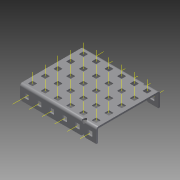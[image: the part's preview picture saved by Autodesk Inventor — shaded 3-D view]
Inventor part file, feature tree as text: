
AUTODESK INVENTOR PART (.ipt)
format: ipt  version: 2015 (Build 190159000, 159)  size: 2,469,376 bytes
history: native  units: in
note: dims shown in document units (in); Inventor stores cm internally (conversion verified against a paired STEP export)
features: other x48, pattern_linear x2, sheet_metal_op x1, extrude x1, imported_body x1, sketch x1
ambient origin geometry x8: Origin, YZ Plane, XZ Plane, XY Plane, X Axis, Y Axis, Z Axis, Center Point
bodies: Body1 (feature_tree)
feature tree (54):
  sheet_metal_op  "Fold1"
  other  "C-Channel"
  extrude  "length cut"  Depth=0.5in
  other  "top axis"
  other  "front axis"
  other  "back axis"
  pattern_linear  "top axes"  Spacing1=0.5in  [1 undecoded]
  pattern_linear  "horiz axes"  Spacing1=0.0in  [1 undecoded]
  other  "right plane"
  imported_body  "Base1"
  sketch  "Sketch1"  dims[d1=0.0in d4=0.5in d5=1.9685in d7=0.5in d10=0.5in d11=0.0in d12=0.0in d13=0.0in d14=-3.0in d15=0.0in d16=0.0in]
  other  "Work Point1"
  other  "Work Axis6"
  other  "Work Axis11"
  other  "Work Axis16"
  other  "Work Axis21"
  other  "Work Point2"
  other  "Work Point3"
  other  "Work Axis36"
  other  "Work Axis37"
  other  "Work Axis38"
  other  "Work Axis39"
  other  "Work Axis40"
  other  "Work Axis60"
  other  "Work Axis61"
  other  "Work Axis62"
  other  "Work Axis63"
  other  "Work Axis64"
  other  "Work Axis84"
  other  "Work Axis85"
  other  "Work Axis86"
  other  "Work Axis87"
  other  "Work Axis88"
  other  "Work Axis108"
  other  "Work Axis109"
  other  "Work Axis110"
  other  "Work Axis111"
  other  "Work Axis112"
  other  "Work Axis132"
  other  "Work Axis133"
  other  "Work Axis134"
  other  "Work Axis135"
  other  "Work Axis136"
  other  "Work Axis156"
  other  "Work Axis157"
  other  "Work Axis158"
  other  "Work Axis159"
  other  "Work Axis160"
  other  "Work Axis180"
  other  "Work Axis181"
  other  "Work Axis182"
  other  "Work Axis183"
  other  "Work Axis184"
  other  "left plane"
note: 2 required parameter values undecoded (feature->parameter linkage not recoverable at this tier; creation-order binding heuristic only, values carry confidence <= 0.55)
